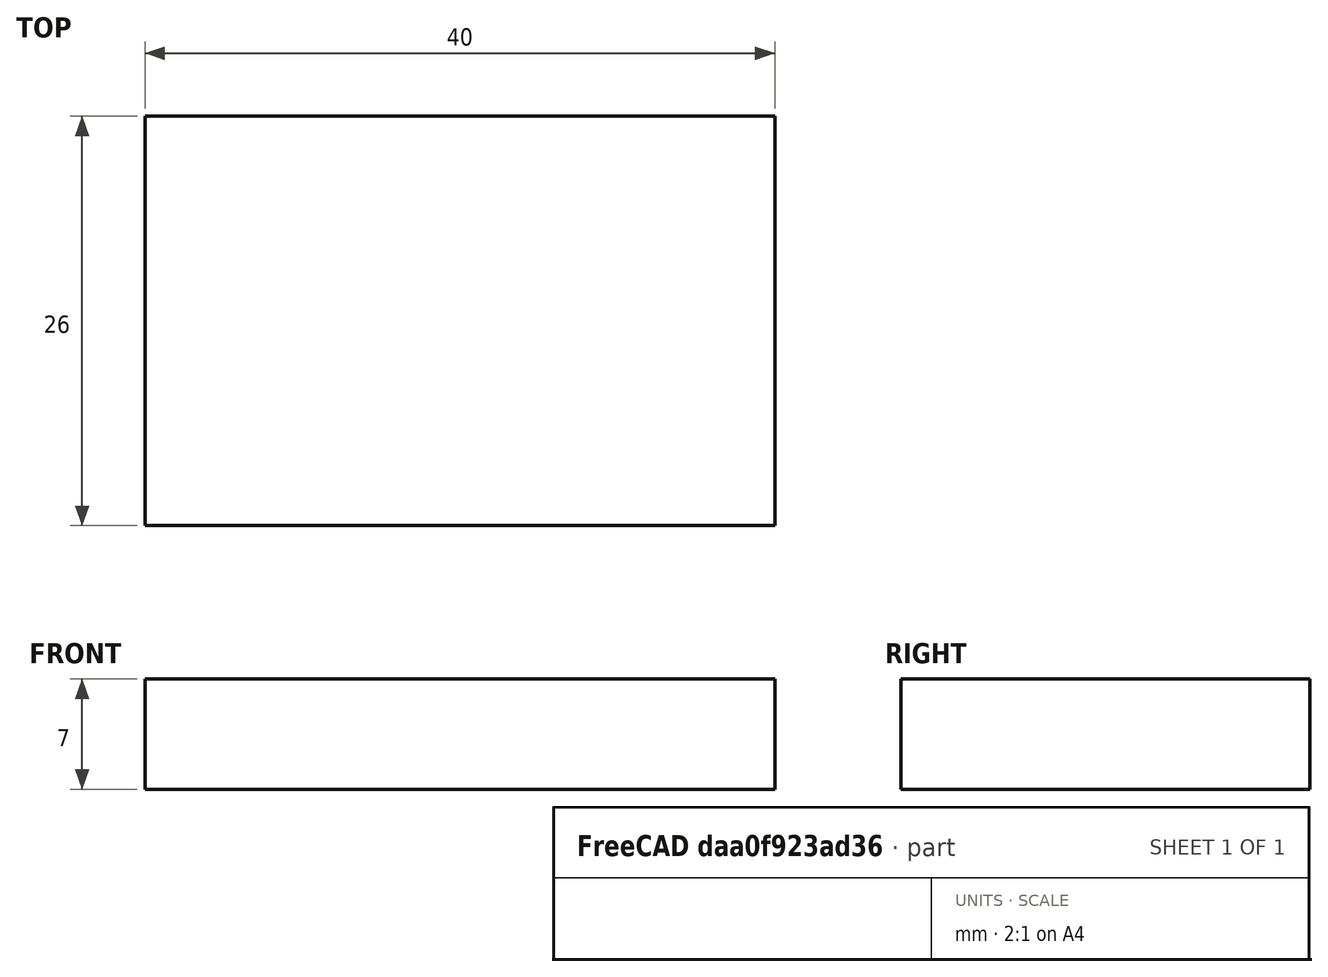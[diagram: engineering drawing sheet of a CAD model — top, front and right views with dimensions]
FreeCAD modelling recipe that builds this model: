
FCSTD DOCUMENT  (FreeCAD 0.17RUnknown)
Label: cam_tail_backup
License: All rights reserved
LicenseURL: http://en.wikipedia.org/wiki/All_rights_reserved
objects: Path::FeaturePython×7, Part::FeaturePython×3, App::FeaturePython×1, Path::FeatureCompoundPython×1
note: 7 computed .brp shape members not serialized (recipe doc carries the construction recipe); baked Part::Feature solids carry a one-line shape summary decoded from their .brp

FEATURE [Path::FeaturePython] Default_Tool  label="Default Tool"  # Path/CAM operation (typed FeaturePython)
  HorizFeed = 3.33333
  HorizRapid = 0
  SpindleDir = 0
  SpindleSpeed = 12000
  ToolNumber = 1
  VertFeed = 1.33333
  VertRapid = 0
  expr: Tool.Diameter = 2
  expr: VertFeed = 80mm / min
  expr: HorizFeed = 200mm / min
  expr: HorizRapid = SetupSheet.HorizRapid
  expr: VertRapid = SetupSheet.VertRapid
FEATURE [Path::FeaturePython] Contour  # Path/CAM operation (typed FeaturePython)
  Active = false
  AreaParams:
    OpenMode = 0
    Angle = 45.0
    MinArcPoints = 4
    Coplanar = 2
    Tolerance = 1e-07
    CleanDistance = 0.0
    PocketExtraOffset = 0.0
    RoundPrecision = 0.0
    AngleShift = 0.0
    SubjectFill = 0
    PocketMode = 0
    Simplify = False
    SectionTolerance = 1e-06
    MaxArcPoints = 100
    Offset = 1.0
    Accuracy = 0.01
    PocketStepover = 0.0
    ClipFill = 0
    ToolRadius = 1.0
    Outline = False
    ClipperScale = 10000000.0
    FromCenter = False
    Explode = False
    EndType = 0
    Shift = 0.0
    ExtraPass = 0
    Project = False
    JoinType = 0
    Thicken = False
    Stepdown = 1.0
    SectionMode = 2
    MiterLimit = 2.0
    Deflection = 0.01
    Reorient = True
    FitArcs = True
    SectionCount = -1
    SectionOffset = 0.0
    Stepover = 0.0
    Unit = 1.0
    Fill = 0
  ClearanceHeight = 2
  Direction = 0
  FinalDepth = -6
  JoinType = 0
  MiterLimit = 0.1
  OffsetExtra = 0
  OpFinalDepth = -7
  OpStartDepth = 0
  OpToolDiameter = 2
  PathParams:
    resume_height = 2.0000000000000053
    feedrate = 3.3333333333333335
    verbose = True
    orientation = 1
    return_end = True
    preamble = False
    retraction = 2.0000000000000053
    feedrate_v = 1.3333333333333333
  SafeHeight = 2
  Side = 0
  StartDepth = 0
  StartPoint = (0,0,0)
  StepDown = 0.1
  ToolController = -> Default_Tool
  UseComp = true
  UseStartPoint = false
  expr: FinalDepth = -6
  expr: ClearanceHeight = StartDepth + SetupSheet.ClearanceHeightOffset
  expr: SafeHeight = StartDepth + SetupSheet.SafeHeightOffset
  expr: StepDown = 0.10000000000000001
  expr: StartDepth = OpStartDepth
FEATURE [App::FeaturePython] SetupSheet  # Path/CAM operation (typed FeaturePython)
  ClearanceHeightExpression = StartDepth+SetupSheet.ClearanceHeightOffset
  ClearanceHeightOffset = 2
  FinalDepthExpression = OpFinalDepth
  HorizRapid = 0
  SafeHeightExpression = StartDepth+SetupSheet.SafeHeightOffset
  SafeHeightOffset = 2
  StartDepthExpression = OpStartDepth
  StepDownExpression = OpToolDiameter
  VertRapid = 0
FEATURE [Part::FeaturePython] tail_01  # a2plus imported part (geometry in sourceFile) (typed FeaturePython)
  fixedPosition = true
  sourceFile = <userpath>/hs/fly/cad/tail.fcstd
  timeLastImport = 1.53696e+09
  updateColors = true
FEATURE [Part::FeaturePython] Clone  label="Base-arm_01"  # Draft clone (typed FeaturePython)
  AttacherType = Attacher::AttachEngine3D
  Fuse = false
  Objects = -> [tail_01]
  PathResource = Base
  Placement = pos=(21,17,-2.5) rot=(1,0,0;-1.5708rad)
  Scale = (1,1,1)
FEATURE [Path::FeaturePython] Pocket_Shape  # Path/CAM operation (typed FeaturePython)
  Active = false
  AreaParams:
    OpenMode = 0
    Angle = 45.0
    MinArcPoints = 4
    Coplanar = 0
    Tolerance = 1e-07
    CleanDistance = 0.0
    PocketExtraOffset = 0.0
    RoundPrecision = 0.0
    AngleShift = 0.0
    SubjectFill = 0
    PocketMode = 2
    Simplify = False
    SectionTolerance = 1e-06
    MaxArcPoints = 100
    Offset = 0.0
    Accuracy = 0.01
    PocketStepover = 1.0
    ClipFill = 0
    ToolRadius = 1.0
    Outline = False
    ClipperScale = 10000000.0
    FromCenter = True
    Explode = False
    EndType = 0
    Shift = 0.0
    ExtraPass = 0
    Project = False
    JoinType = 0
    Thicken = False
    Stepdown = 1.0
    SectionMode = 2
    MiterLimit = 2.0
    Deflection = 0.01
    Reorient = True
    FitArcs = True
    SectionCount = -1
    SectionOffset = 0.0
    Stepover = 0.0
    Unit = 1.0
    Fill = 0
  Base = -> [Clone]
  ClearanceHeight = 2
  CutMode = 0
  ExtraOffset = 0
  FinalDepth = -3
  FinishDepth = 0
  KeepToolDown = false
  MinTravel = false
  OffsetPattern = 1
  OpFinalDepth = -3
  OpStartDepth = 0
  OpToolDiameter = 2
  PathParams = {'resume_height': 2.0, 'feedrate': 3.3333333333333335, 'verbose': True, 'orientation': 1, 'return_end': True, 'preamble': False, 'retraction': 2.0, 'feedrate_v': 1.3333333333333333}
  SafeHeight = 2
  StartAt = 0
  StartDepth = 0
  StartPoint = (0,0,0)
  StepDown = 0.1
  StepOver = 50
  ToolController = -> Default_Tool
  UseStartPoint = false
  ZigZagAngle = 45
  expr: ClearanceHeight = StartDepth + SetupSheet.ClearanceHeightOffset
  expr: SafeHeight = StartDepth + SetupSheet.SafeHeightOffset
  expr: StepDown = 0.10000000000000001
  expr: FinalDepth = -3
  expr: StartDepth = 0
FEATURE [Part::FeaturePython] Stock  # WARN: FeaturePython — macro-defined, semantics opaque (R4)
  Base = -> tail_01
  ExtXneg = 1
  ExtXpos = 1
  ExtYneg = 1
  ExtYpos = 1
  ExtZneg = 1
  ExtZpos = 1
  Placement = pos=(21,17,-3.5) rot=(1,0,0;4.71239rad)
  StockType = FromBase
FEATURE [Path::FeaturePython] Pocket_Shape001  # Path/CAM operation (typed FeaturePython)
  Active = true
  AreaParams:
    OpenMode = 0
    Angle = 45.0
    MinArcPoints = 4
    Coplanar = 0
    Tolerance = 1e-07
    CleanDistance = 0.0
    PocketExtraOffset = 0.0
    RoundPrecision = 0.0
    AngleShift = 0.0
    SubjectFill = 0
    PocketMode = 2
    Simplify = False
    SectionTolerance = 1e-06
    MaxArcPoints = 100
    Offset = 0.0
    Accuracy = 0.01
    PocketStepover = 1.0
    ClipFill = 0
    ToolRadius = 1.0
    Outline = False
    ClipperScale = 10000000.0
    FromCenter = True
    Explode = False
    EndType = 0
    Shift = 0.0
    ExtraPass = 0
    Project = False
    JoinType = 0
    Thicken = False
    Stepdown = 1.0
    SectionMode = 2
    MiterLimit = 2.0
    Deflection = 0.01
    Reorient = True
    FitArcs = True
    SectionCount = -1
    SectionOffset = 0.0
    Stepover = 0.0
    Unit = 1.0
    Fill = 0
  Base = -> [Clone]
  ClearanceHeight = -1
  CutMode = 0
  ExtraOffset = 0
  FinalDepth = -6
  FinishDepth = 0
  KeepToolDown = false
  MinTravel = false
  OffsetPattern = 1
  OpFinalDepth = -5
  OpStartDepth = 0
  OpToolDiameter = 2
  PathParams = {'resume_height': -1.0, 'feedrate': 3.3333333333333335, 'verbose': True, 'orientation': 1, 'return_end': True, 'preamble': False, 'retraction': -1.0, 'feedrate_v': 1.3333333333333333}
  SafeHeight = -1
  StartAt = 0
  StartDepth = -3
  StartPoint = (0,0,0)
  StepDown = 0.1
  StepOver = 50
  ToolController = -> Default_Tool
  UseStartPoint = false
  ZigZagAngle = 45
  expr: ClearanceHeight = StartDepth + SetupSheet.ClearanceHeightOffset
  expr: SafeHeight = StartDepth + SetupSheet.SafeHeightOffset
  expr: StepDown = 0.10000000000000001
  expr: FinalDepth = -6
  expr: StartDepth = -3
FEATURE [Path::FeaturePython] TagDressup  # Path/CAM operation (typed FeaturePython)
  Angle = 45
  Base = -> Contour
  Height = 3
  Positions = (2) [(1,17.15,0),(41,16.59,0)]
  Radius = 0
  SegmentationFactor = 50
  Width = 3.8
FEATURE [Path::FeaturePython] Pocket_Shape002  # Path/CAM operation (typed FeaturePython)
  Active = true
  AreaParams:
    OpenMode = 0
    Angle = 45.0
    MinArcPoints = 4
    Coplanar = 0
    Tolerance = 1e-07
    CleanDistance = 0.0
    PocketExtraOffset = 0.0
    RoundPrecision = 0.0
    AngleShift = 0.0
    SubjectFill = 0
    PocketMode = 2
    Simplify = False
    SectionTolerance = 1e-06
    MaxArcPoints = 100
    Offset = 0.0
    Accuracy = 0.01
    PocketStepover = 2.0
    ClipFill = 0
    ToolRadius = 1.0
    Outline = False
    ClipperScale = 10000000.0
    FromCenter = True
    Explode = False
    EndType = 0
    Shift = 0.0
    ExtraPass = 0
    Project = False
    JoinType = 0
    Thicken = False
    Stepdown = 1.0
    SectionMode = 2
    MiterLimit = 2.0
    Deflection = 0.01
    Reorient = True
    FitArcs = True
    SectionCount = -1
    SectionOffset = 0.0
    Stepover = 0.0
    Unit = 1.0
    Fill = 0
  Base = -> [Clone]
  ClearanceHeight = -1
  CutMode = 0
  ExtraOffset = 0
  FinalDepth = -5.6
  FinishDepth = 0
  KeepToolDown = false
  MinTravel = false
  OffsetPattern = 1
  OpFinalDepth = -5
  OpStartDepth = 0
  OpToolDiameter = 2
  PathParams = {'resume_height': -1.0, 'feedrate': 3.3333333333333335, 'verbose': True, 'orientation': 1, 'return_end': True, 'preamble': False, 'retraction': -1.0, 'feedrate_v': 1.3333333333333333}
  SafeHeight = -1
  StartAt = 0
  StartDepth = -3
  StartPoint = (0,0,0)
  StepDown = 0.1
  StepOver = 100
  ToolController = -> Default_Tool
  UseStartPoint = false
  ZigZagAngle = 45
  expr: ClearanceHeight = StartDepth + SetupSheet.ClearanceHeightOffset
  expr: SafeHeight = StartDepth + SetupSheet.SafeHeightOffset
  expr: StepDown = 0.10000000000000001
  expr: FinalDepth = -5.5999999999999996
  expr: StartDepth = -3
FEATURE [Path::FeatureCompoundPython] Operations  # Path/CAM operation (typed FeaturePython)
  Group = -> [Pocket_Shape,Pocket_Shape001,TagDressup,Pocket_Shape002]
  UsePlacements = false
FEATURE [Path::FeaturePython] Job  # Path/CAM operation (typed FeaturePython)
  Base = -> Clone
  GeometryTolerance = 0.01
  Operations = -> Operations
  PostProcessor = 5
  PostProcessorOutputFile = <userpath>/hs/fly/cad/gcode/arm
  SetupSheet = -> SetupSheet
  Stock = -> Stock
  ToolController = -> [Default_Tool]
